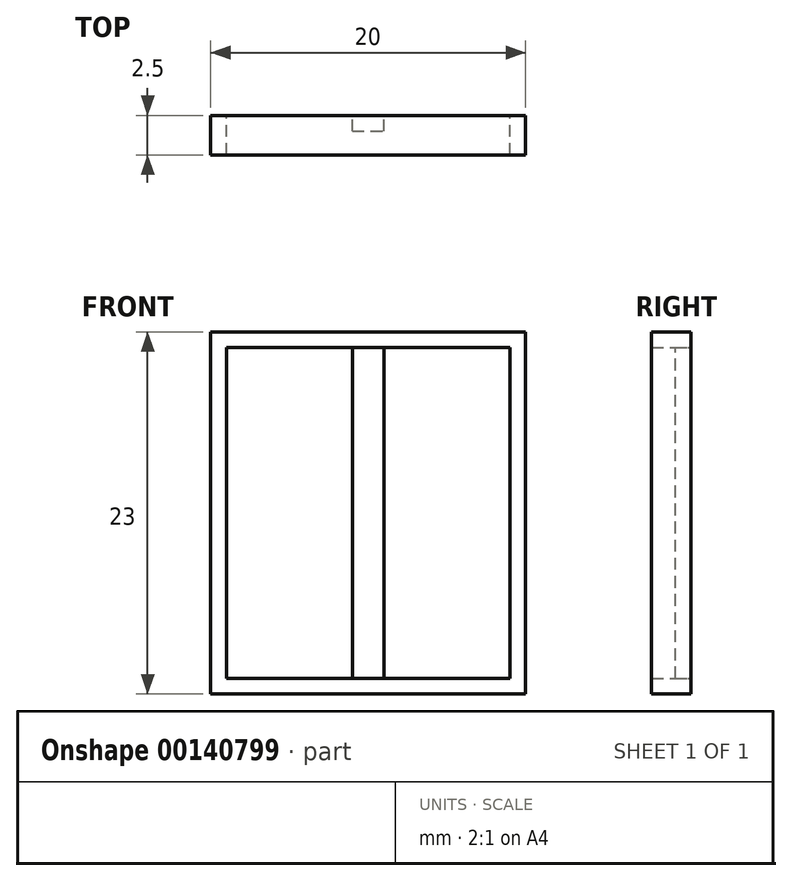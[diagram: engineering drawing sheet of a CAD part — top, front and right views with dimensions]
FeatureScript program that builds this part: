
annotation { "Feature Type Name" : "Feature", "Feature Type Description" : "" }
export const myFeature = defineFeature(function(context is Context, id is Id, definition is map)
    precondition{}
    {
        {
            var Q0;
            Q0=qCreatedBy(makeId("Front.planeOp"),FACE);
            var sketch = newSketch(context, id + "F0", { "sketchPlane" : qUnion([Q0])});
            skLineSegment(sketch, "E0.bottom", {"start": v(-10.6, 9.48) * mm, "end": v(9.4, 9.48) * mm});
            skLineSegment(sketch, "E0.top", {"start": v(-10.6, -13.52) * mm, "end": v(9.4, -13.52) * mm});
            skLineSegment(sketch, "E0.left", {"start": v(-10.6, 9.48) * mm, "end": v(-10.6, -13.52) * mm});
            skLineSegment(sketch, "E0.right", {"start": v(9.4, 9.48) * mm, "end": v(9.4, -13.52) * mm});
            skLineSegment(sketch, "E1.0", {"start": v(-9.6, 8.48) * mm, "end": v(8.4, 8.48) * mm});
            skLineSegment(sketch, "E1.1", {"start": v(-9.6, 8.48) * mm, "end": v(-9.6, -12.52) * mm});
            skLineSegment(sketch, "E1.2", {"start": v(-9.6, -12.52) * mm, "end": v(8.4, -12.52) * mm});
            skLineSegment(sketch, "E1.3", {"start": v(8.4, 8.48) * mm, "end": v(8.4, -12.52) * mm});
            skLineSegment(sketch, "E2", {"start": v(-0.6, -12.52) * mm, "end": v(-0.6, 8.48) * mm});
            skLineSegment(sketch, "E3.0", {"start": v(-1.6, -12.52) * mm, "end": v(-1.6, 8.48) * mm});
            skLineSegment(sketch, "E4.0", {"start": v(0.4, -12.52) * mm, "end": v(0.4, 8.48) * mm});
            skLineSegment(sketch, "E5", {"start": v(-9.6, 2.48) * mm, "end": v(8.4, 2.48) * mm});
            skLineSegment(sketch, "E6", {"start": v(-9.6, -6.52) * mm, "end": v(8.4, -6.52) * mm});
            skLineSegment(sketch, "E7.0", {"start": v(-9.6, 1.48) * mm, "end": v(8.4, 1.48) * mm});
            skLineSegment(sketch, "E8.0", {"start": v(-9.6, -5.52) * mm, "end": v(8.4, -5.52) * mm});
            skSolve(sketch);
        }
        {
            var Q0;
            Q0=makeQuery(id+"F0.imprint","IMPRINT",FACE,{"disambiguationData":[TD([[makeQuery(id+"F0.imprint","IMPRINT",EDGE,{"derivedFrom":sQuery(id+"F0.wireOp",EDGE,"E0.bottom")}),-1.0]])]});
            extrude(context, id + "F1", {"entities" : qUnion([Q0]), "depth" : 2.5 * mm});
        }
        {
            var Q0;
            {var subQ0=sQuery(id+"F0.wireOp",EDGE,"E8.0");var subQ1=sQuery(id+"F0.wireOp",EDGE,"E2");var subQ2=makeQuery(id+"F0.imprint","INTERSECT",VERTEX,{"derivedFrom":[subQ1,subQ0]});Q0=makeQuery(id+"F0.imprint","IMPRINT",FACE,{"disambiguationData":[TD([[makeQuery(id+"F0.imprint","IMPRINT",EDGE,{"disambiguationData":[TD([[subQ2,-1.0]])],"derivedFrom":subQ1}),1.0]])]});}
            var Q1;
            {var subQ0=sQuery(id+"F0.wireOp",EDGE,"E2");var subQ1=sQuery(id+"F0.wireOp",EDGE,"E1.2");var subQ2=makeQuery(id+"F0.imprint","INTERSECT",VERTEX,{"derivedFrom":[subQ1,subQ0]});Q1=makeQuery(id+"F0.imprint","IMPRINT",FACE,{"disambiguationData":[TD([[makeQuery(id+"F0.imprint","IMPRINT",EDGE,{"disambiguationData":[TD([[subQ2,1.0]])],"derivedFrom":subQ1}),1.0]])]});}
            var Q2;
            {var subQ0=sQuery(id+"F0.wireOp",EDGE,"E2");var subQ1=sQuery(id+"F0.wireOp",EDGE,"E1.2");var subQ2=makeQuery(id+"F0.imprint","INTERSECT",VERTEX,{"derivedFrom":[subQ1,subQ0]});Q2=makeQuery(id+"F0.imprint","IMPRINT",FACE,{"disambiguationData":[TD([[makeQuery(id+"F0.imprint","IMPRINT",EDGE,{"disambiguationData":[TD([[subQ2,-1.0]])],"derivedFrom":subQ1}),1.0]])]});}
            var Q3;
            {var subQ0=sQuery(id+"F0.wireOp",EDGE,"E2");var subQ1=sQuery(id+"F0.wireOp",EDGE,"E1.0");var subQ2=makeQuery(id+"F0.imprint","INTERSECT",VERTEX,{"derivedFrom":[subQ1,subQ0]});Q3=makeQuery(id+"F0.imprint","IMPRINT",FACE,{"disambiguationData":[TD([[makeQuery(id+"F0.imprint","IMPRINT",EDGE,{"disambiguationData":[TD([[subQ2,1.0]])],"derivedFrom":subQ1}),-1.0]])]});}
            var Q4;
            {var subQ0=sQuery(id+"F0.wireOp",EDGE,"E2");var subQ1=sQuery(id+"F0.wireOp",EDGE,"E1.0");var subQ2=makeQuery(id+"F0.imprint","INTERSECT",VERTEX,{"derivedFrom":[subQ1,subQ0]});Q4=makeQuery(id+"F0.imprint","IMPRINT",FACE,{"disambiguationData":[TD([[makeQuery(id+"F0.imprint","IMPRINT",EDGE,{"disambiguationData":[TD([[subQ2,-1.0]])],"derivedFrom":subQ1}),-1.0]])]});}
            var Q5;
            {var subQ0=sQuery(id+"F0.wireOp",EDGE,"E7.0");var subQ1=sQuery(id+"F0.wireOp",EDGE,"E2");var subQ2=makeQuery(id+"F0.imprint","INTERSECT",VERTEX,{"derivedFrom":[subQ1,subQ0]});Q5=makeQuery(id+"F0.imprint","IMPRINT",FACE,{"disambiguationData":[TD([[makeQuery(id+"F0.imprint","IMPRINT",EDGE,{"disambiguationData":[TD([[subQ2,-1.0]])],"derivedFrom":subQ1}),1.0]])]});}
            var Q6;
            {var subQ0=sQuery(id+"F0.wireOp",EDGE,"E7.0");var subQ1=sQuery(id+"F0.wireOp",EDGE,"E2");var subQ2=makeQuery(id+"F0.imprint","INTERSECT",VERTEX,{"derivedFrom":[subQ1,subQ0]});Q6=makeQuery(id+"F0.imprint","IMPRINT",FACE,{"disambiguationData":[TD([[makeQuery(id+"F0.imprint","IMPRINT",EDGE,{"disambiguationData":[TD([[subQ2,-1.0]])],"derivedFrom":subQ1}),-1.0]])]});}
            var Q7;
            {var subQ0=sQuery(id+"F0.wireOp",EDGE,"E8.0");var subQ1=sQuery(id+"F0.wireOp",EDGE,"E2");var subQ2=makeQuery(id+"F0.imprint","INTERSECT",VERTEX,{"derivedFrom":[subQ1,subQ0]});Q7=makeQuery(id+"F0.imprint","IMPRINT",FACE,{"disambiguationData":[TD([[makeQuery(id+"F0.imprint","IMPRINT",EDGE,{"disambiguationData":[TD([[subQ2,-1.0]])],"derivedFrom":subQ1}),-1.0]])]});}
            var Q8;
            {var subQ0=sQuery(id+"F0.wireOp",EDGE,"E6");var subQ1=sQuery(id+"F0.wireOp",EDGE,"E2");var subQ2=makeQuery(id+"F0.imprint","INTERSECT",VERTEX,{"derivedFrom":[subQ1,subQ0]});Q8=makeQuery(id+"F0.imprint","IMPRINT",FACE,{"disambiguationData":[TD([[makeQuery(id+"F0.imprint","IMPRINT",EDGE,{"disambiguationData":[TD([[subQ2,-1.0]])],"derivedFrom":subQ1}),-1.0]])]});}
            var Q9;
            {var subQ0=sQuery(id+"F0.wireOp",EDGE,"E6");var subQ1=sQuery(id+"F0.wireOp",EDGE,"E2");var subQ2=makeQuery(id+"F0.imprint","INTERSECT",VERTEX,{"derivedFrom":[subQ1,subQ0]});Q9=makeQuery(id+"F0.imprint","IMPRINT",FACE,{"disambiguationData":[TD([[makeQuery(id+"F0.imprint","IMPRINT",EDGE,{"disambiguationData":[TD([[subQ2,-1.0]])],"derivedFrom":subQ1}),1.0]])]});}
            extrude(context, id + "F2", {"entities" : qUnion([Q0, Q1, Q2, Q3, Q4, Q5, Q6, Q7, Q8, Q9]), "operationType" : NewBodyOperationType.ADD, "depth" : 1 * mm});
        }
    });
